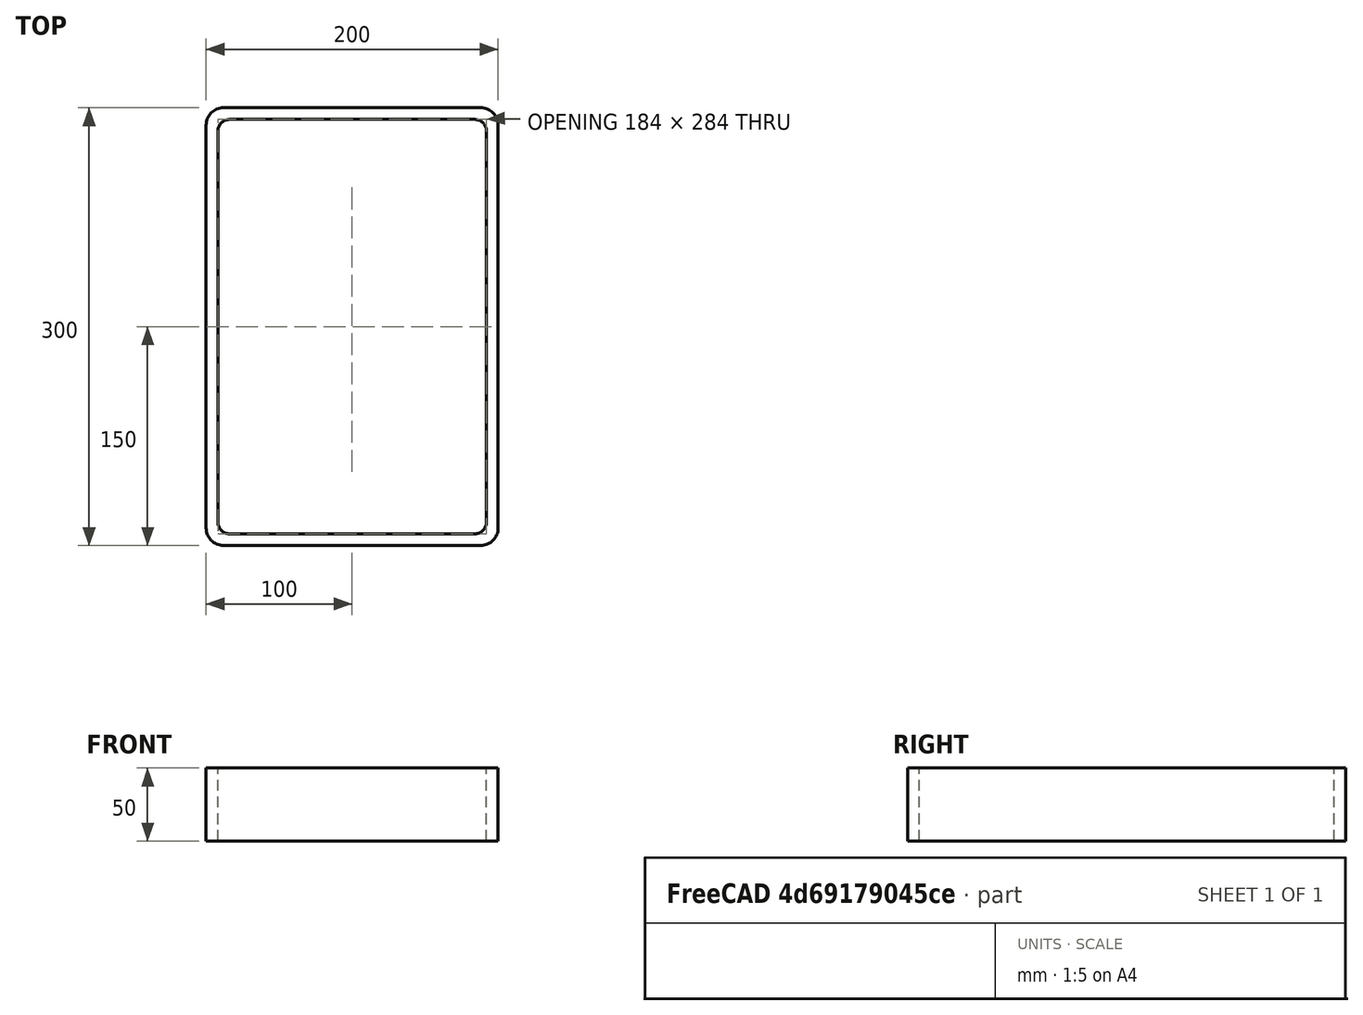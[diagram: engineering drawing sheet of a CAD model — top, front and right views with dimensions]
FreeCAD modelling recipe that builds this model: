
FCSTD DOCUMENT  (FreeCAD 0.15R4671 (Git))
Label: Rectangular hollow section 300x200x8 EN10219 S235JRH
License: All rights reserved
LicenseURL: http://en.wikipedia.org/wiki/All_rights_reserved
objects: Sketcher::SketchObject×1, Part::Extrusion×1
note: 2 computed .brp shape members not serialized (recipe doc carries the construction recipe); baked Part::Feature solids carry a one-line shape summary decoded from their .brp

FEATURE [Sketcher::SketchObject] Sketch
  sketch-geometry (16):
    g0: LineSegment StartX=-84 StartY=142 StartZ=0 EndX=84 EndY=142 EndZ=0
    g1: LineSegment StartX=92 StartY=134 StartZ=0 EndX=92 EndY=-134 EndZ=0
    g2: LineSegment StartX=84 StartY=-142 StartZ=0 EndX=-84 EndY=-142 EndZ=0
    g3: LineSegment StartX=-92 StartY=-134 StartZ=0 EndX=-92 EndY=134 EndZ=0
    g4: LineSegment StartX=-88 StartY=150 StartZ=0 EndX=88 EndY=150 EndZ=0
    g5: LineSegment StartX=100 StartY=138 StartZ=0 EndX=100 EndY=-138 EndZ=0
    g6: LineSegment StartX=88 StartY=-150 StartZ=0 EndX=-88 EndY=-150 EndZ=0
    g7: LineSegment StartX=-100 StartY=-138 StartZ=0 EndX=-100 EndY=138 EndZ=0
    g8: ArcOfCircle CenterX=-84 CenterY=134 CenterZ=0 NormalX=0 NormalY=0 NormalZ=1 Radius=8 StartAngle=1.5708 EndAngle=3.14159
    g9: ArcOfCircle CenterX=84 CenterY=134 CenterZ=0 NormalX=0 NormalY=0 NormalZ=1 Radius=8 StartAngle=0 EndAngle=1.5708
    g10: ArcOfCircle CenterX=84 CenterY=-134 CenterZ=0 NormalX=0 NormalY=0 NormalZ=1 Radius=8 StartAngle=4.71239 EndAngle=6.28319
    g11: ArcOfCircle CenterX=-84 CenterY=-134 CenterZ=0 NormalX=0 NormalY=0 NormalZ=1 Radius=8 StartAngle=3.14159 EndAngle=4.71239
    g12: ArcOfCircle CenterX=88 CenterY=138 CenterZ=0 NormalX=0 NormalY=0 NormalZ=1 Radius=12 StartAngle=0 EndAngle=1.5708
    g13: ArcOfCircle CenterX=88 CenterY=-138 CenterZ=0 NormalX=0 NormalY=0 NormalZ=1 Radius=12 StartAngle=4.71239 EndAngle=6.28319
    g14: ArcOfCircle CenterX=-88 CenterY=-138 CenterZ=0 NormalX=0 NormalY=0 NormalZ=1 Radius=12 StartAngle=3.14159 EndAngle=4.71239
    g15: ArcOfCircle CenterX=-88 CenterY=138 CenterZ=0 NormalX=0 NormalY=0 NormalZ=1 Radius=12 StartAngle=1.5708 EndAngle=3.14159
  constraints (36):
    c: Horizontal(g2)
    c: Vertical(g3)
    c: Horizontal(g6)
    c: Vertical(g7)
    c: Tangent(g3,g8) = 1.5708
    c: Tangent(g0,g8) = 1.5708
    c: Tangent(g0,g9) = 1.5708
    c: Tangent(g1,g9) = 1.5708
    c: Tangent(g1,g10) = 1.5708
    c: Tangent(g2,g10) = 1.5708
    c: Tangent(g2,g11) = 1.5708
    c: Tangent(g3,g11) = 1.5708
    c: Tangent(g4,g12) = 1.5708
    c: Tangent(g5,g12) = 1.5708
    c: Tangent(g5,g13) = 1.5708
    c: Tangent(g6,g13) = 1.5708
    c: Tangent(g6,g14) = 1.5708
    c: Tangent(g7,g14) = 1.5708
    c: Tangent(g7,g15) = 1.5708
    c: Tangent(g4,g15) = 1.5708
    c: Equal(g9,g8)
    c: Equal(g9,g11)
    c: Equal(g9,g10)
    c: Equal(g12,g15)
    c: Equal(g12,g14)
    c: Equal(g12,g13)
    c: Symmetric(g4,g6,g-1)
    c: Symmetric(g7,g5,g-2)
    c: DistanceY(g4,g6) = -300
    c: DistanceX(g7,g5) = 200
    c: Symmetric(g3,g1,g-2)
    c: Symmetric(g0,g2,g-1)
    c: DistanceY(g0,g4) = 8
    c: DistanceX(g5,g1) = -8
    c: Radius(g9) = 8
    c: Radius(g12) = 12
FEATURE [Part::Extrusion] Extrude  label="Rectangular hollow section 300x200x8 EN10219 S235JRH"
  Base = -> Sketch
  Dir = (0,0,50)
  Solid = true
